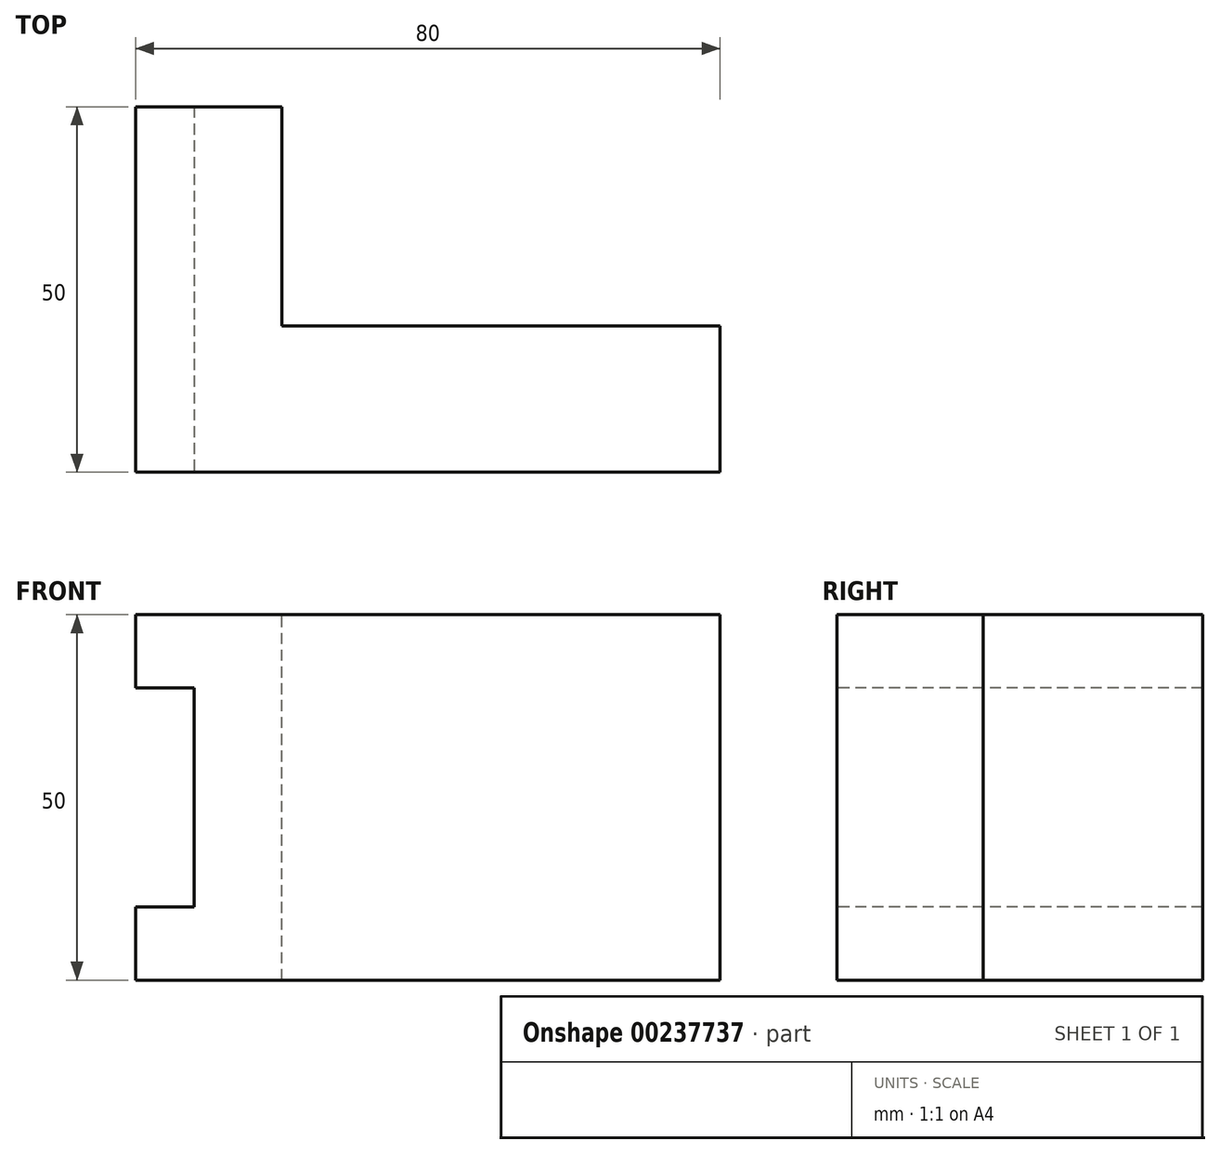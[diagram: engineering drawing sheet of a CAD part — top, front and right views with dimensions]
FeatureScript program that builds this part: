
annotation { "Feature Type Name" : "Feature", "Feature Type Description" : "" }
export const myFeature = defineFeature(function(context is Context, id is Id, definition is map)
    precondition{}
    {
        {
            var Q0;
            Q0=qCreatedBy(makeId("Front.planeOp"),FACE);
            var sketch = newSketch(context, id + "F0", { "sketchPlane" : qUnion([Q0])});
            skLineSegment(sketch, "E0.bottom", {"start": v(60, 0) * mm, "end": v(0, 0) * mm});
            skLineSegment(sketch, "E0.top", {"start": v(60, 50) * mm, "end": v(0, 50) * mm});
            skLineSegment(sketch, "E0.left", {"start": v(60, 0) * mm, "end": v(60, 50) * mm});
            skLineSegment(sketch, "E0.right", {"start": v(0, 0) * mm, "end": v(0, 50) * mm});
            skLineSegment(sketch, "E1.bottom", {"start": v(0, 50) * mm, "end": v(-20, 50) * mm});
            skLineSegment(sketch, "E1.top", {"start": v(0, 0) * mm, "end": v(-20, 0) * mm});
            skLineSegment(sketch, "E1.left", {"start": v(0, 50) * mm, "end": v(0, 0) * mm});
            skLineSegment(sketch, "E1.right", {"start": v(-20, 50) * mm, "end": v(-20, 0) * mm});
            skLineSegment(sketch, "E2.bottom", {"start": v(-20, 40) * mm, "end": v(-12, 40) * mm});
            skLineSegment(sketch, "E2.top", {"start": v(-20, 10) * mm, "end": v(-12, 10) * mm});
            skLineSegment(sketch, "E2.left", {"start": v(-20, 40) * mm, "end": v(-20, 10) * mm});
            skLineSegment(sketch, "E2.right", {"start": v(-12, 40) * mm, "end": v(-12, 10) * mm});
            skSolve(sketch);
        }
        {
            var Q0;
            Q0=makeQuery(id+"F0.imprint","IMPRINT",FACE,{"disambiguationData":[TD([[makeQuery(id+"F0.imprint","IMPRINT",EDGE,{"derivedFrom":sQuery(id+"F0.wireOp",EDGE,"E0.bottom")}),-1.0]])]});
            extrude(context, id + "F1", {"entities" : qUnion([Q0]), "oppositeDirection" : true, "depth" : 20 * mm});
        }
        {
            var Q0;
            {var subQ1=sQuery(id+"F0.wireOp",EDGE,"E1.bottom");Q0=makeQuery(id+"F0.imprint","IMPRINT",FACE,{"disambiguationData":[TD([[makeQuery(id+"F0.imprint","IMPRINT",EDGE,{"derivedFrom":subQ1}),1.0]])]});}
            extrude(context, id + "F2", {"entities" : qUnion([Q0]), "operationType" : NewBodyOperationType.ADD, "oppositeDirection" : true, "depth" : 50 * mm});
        }
    });
